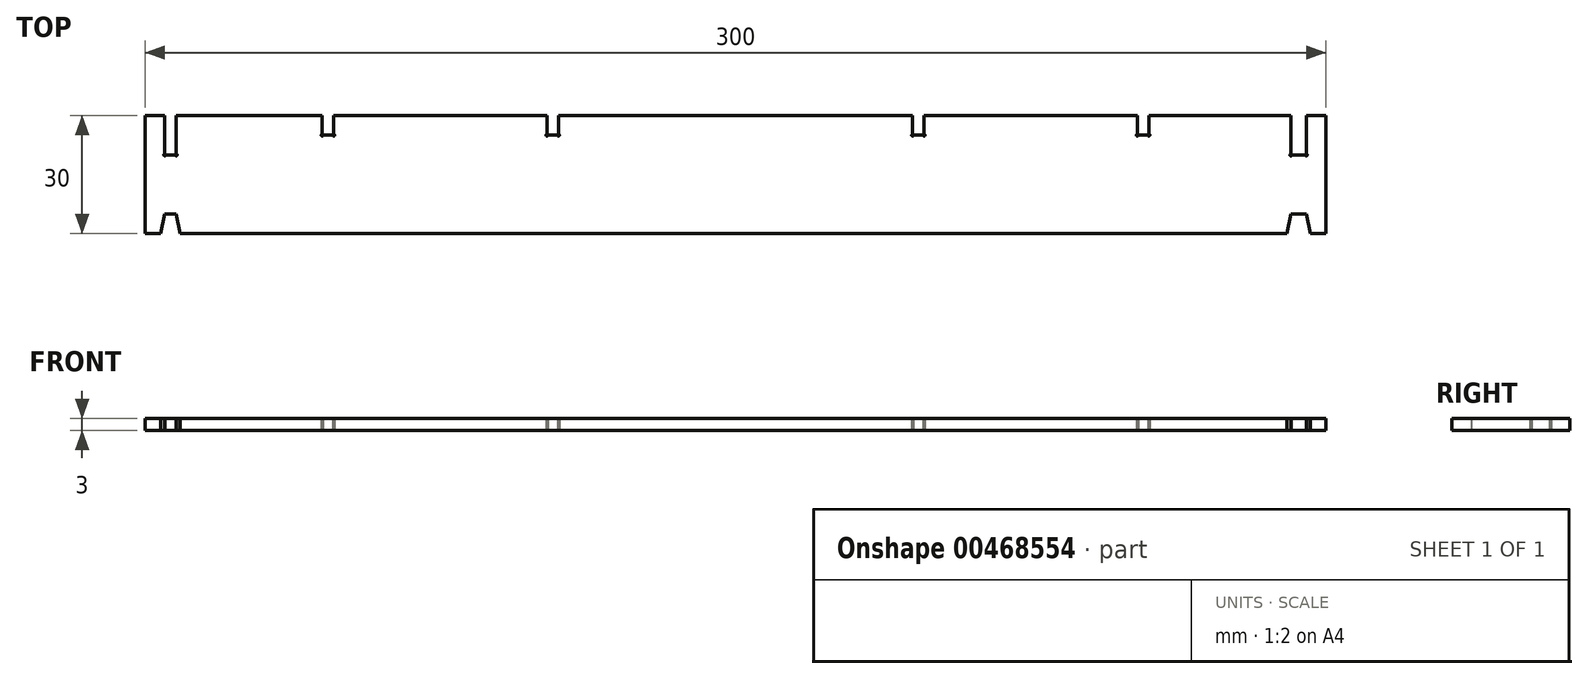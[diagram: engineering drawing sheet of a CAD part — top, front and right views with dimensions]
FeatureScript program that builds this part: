
annotation { "Feature Type Name" : "Feature", "Feature Type Description" : "" }
export const myFeature = defineFeature(function(context is Context, id is Id, definition is map)
    precondition{}
    {
        {
            var Q0;
            Q0=qCreatedBy(makeId("Top.planeOp"),FACE);
            var sketch = newSketch(context, id + "F0", { "sketchPlane" : qUnion([Q0])});
            skLineSegment(sketch, "E0.bottom", {"start": v(-145.05, -9.99) * mm, "end": v(154.95, -9.99) * mm});
            skLineSegment(sketch, "E0.top", {"start": v(-145.05, -39.99) * mm, "end": v(154.95, -39.99) * mm});
            skLineSegment(sketch, "E0.left", {"start": v(-145.05, -9.99) * mm, "end": v(-145.05, -39.99) * mm});
            skLineSegment(sketch, "E0.right", {"start": v(154.95, -9.99) * mm, "end": v(154.95, -39.99) * mm});
            skPoint(sketch, "E1", {"position": v(-100.05, -9.99) * mm});
            skPoint(sketch, "E2", {"position": v(109.95, -9.99) * mm});
            skLineSegment(sketch, "E3", {"start": v(109.95, -9.99) * mm, "end": v(109.95, -14.99) * mm});
            skLineSegment(sketch, "E4", {"start": v(109.95, -14.99) * mm, "end": v(107.05, -14.99) * mm});
            skLineSegment(sketch, "E5", {"start": v(107.05, -14.99) * mm, "end": v(107.05, -9.99) * mm});
            skLineSegment(sketch, "E6", {"start": v(-100.05, -9.99) * mm, "end": v(-100.05, -14.99) * mm});
            skLineSegment(sketch, "E7", {"start": v(-100.05, -14.99) * mm, "end": v(-97.15, -14.99) * mm});
            skLineSegment(sketch, "E8", {"start": v(-97.15, -14.99) * mm, "end": v(-97.15, -9.99) * mm});
            skPoint(sketch, "E9", {"position": v(-40.05, -9.99) * mm});
            skLineSegment(sketch, "E10", {"start": v(-40.05, -9.99) * mm, "end": v(-40.05, -14.99) * mm});
            skLineSegment(sketch, "E11", {"start": v(-40.05, -14.99) * mm, "end": v(-42.95, -14.99) * mm});
            skLineSegment(sketch, "E12", {"start": v(-42.95, -14.99) * mm, "end": v(-42.95, -9.99) * mm});
            skPoint(sketch, "E13", {"position": v(49.95, -9.99) * mm});
            skLineSegment(sketch, "E14", {"start": v(49.95, -9.99) * mm, "end": v(49.95, -14.99) * mm});
            skLineSegment(sketch, "E15", {"start": v(49.95, -14.99) * mm, "end": v(52.85, -14.99) * mm});
            skLineSegment(sketch, "E16", {"start": v(52.85, -14.99) * mm, "end": v(52.85, -9.99) * mm});
            skPoint(sketch, "E17", {"position": v(-140.05, -9.99) * mm});
            skLineSegment(sketch, "E18", {"start": v(-140.05, -9.99) * mm, "end": v(-140.05, -19.99) * mm});
            skLineSegment(sketch, "E19", {"start": v(-140.05, -19.99) * mm, "end": v(-137.15, -19.99) * mm});
            skLineSegment(sketch, "E20", {"start": v(-137.15, -19.99) * mm, "end": v(-137.15, -9.99) * mm});
            skLineSegment(sketch, "E21", {"start": v(149.95, -9.99) * mm, "end": v(149.95, -19.99) * mm});
            skLineSegment(sketch, "E22", {"start": v(149.95, -19.99) * mm, "end": v(146.05, -19.99) * mm});
            skLineSegment(sketch, "E23", {"start": v(146.05, -19.99) * mm, "end": v(146.05, -9.99) * mm});
            skCircle(sketch, "E24", {"center": v(-140.05, -19.99) * mm, "radius": 0.25 * mm});
            skCircle(sketch, "E25", {"center": v(-137.15, -19.99) * mm, "radius": 0.25 * mm});
            skCircle(sketch, "E26", {"center": v(-100.05, -14.99) * mm, "radius": 0.25 * mm});
            skCircle(sketch, "E27", {"center": v(-97.15, -14.99) * mm, "radius": 0.25 * mm});
            skCircle(sketch, "E28", {"center": v(-42.95, -14.99) * mm, "radius": 0.25 * mm});
            skCircle(sketch, "E29", {"center": v(-40.05, -14.99) * mm, "radius": 0.25 * mm});
            skCircle(sketch, "E30", {"center": v(49.95, -14.99) * mm, "radius": 0.25 * mm});
            skCircle(sketch, "E31", {"center": v(52.85, -14.99) * mm, "radius": 0.25 * mm});
            skCircle(sketch, "E32", {"center": v(107.05, -14.99) * mm, "radius": 0.25 * mm});
            skCircle(sketch, "E33", {"center": v(109.95, -14.99) * mm, "radius": 0.25 * mm});
            skCircle(sketch, "E34", {"center": v(146.05, -19.99) * mm, "radius": 0.25 * mm});
            skCircle(sketch, "E35", {"center": v(149.95, -19.99) * mm, "radius": 0.25 * mm});
            skLineSegment(sketch, "E36", {"start": v(-140.05, -9.99) * mm, "end": v(-140.05, -39.99) * mm, "construction": true});
            skLineSegment(sketch, "E37", {"start": v(-137.15, -9.99) * mm, "end": v(-137.15, -39.99) * mm, "construction": true});
            skLineSegment(sketch, "E38", {"start": v(149.95, -9.99) * mm, "end": v(149.95, -39.99) * mm, "construction": true});
            skLineSegment(sketch, "E39", {"start": v(146.05, -9.99) * mm, "end": v(146.05, -39.99) * mm, "construction": true});
            skLineSegment(sketch, "E40", {"start": v(150.95, -39.99) * mm, "end": v(149.95, -34.99) * mm});
            skLineSegment(sketch, "E41", {"start": v(149.95, -34.99) * mm, "end": v(146.05, -34.99) * mm});
            skLineSegment(sketch, "E42", {"start": v(146.05, -34.99) * mm, "end": v(145.05, -39.99) * mm});
            skLineSegment(sketch, "E43", {"start": v(-141.05, -39.99) * mm, "end": v(-140.05, -34.99) * mm});
            skLineSegment(sketch, "E44", {"start": v(-140.05, -34.99) * mm, "end": v(-137.15, -34.99) * mm});
            skLineSegment(sketch, "E45", {"start": v(-137.15, -34.99) * mm, "end": v(-136.15, -39.99) * mm});
            skSolve(sketch);
        }
        {
            var Q0;
            Q0=makeQuery(id+"F0.imprint","IMPRINT",FACE,{"disambiguationData":[TD([[makeQuery(id+"F0.imprint","IMPRINT",EDGE,{"derivedFrom":sQuery(id+"F0.wireOp",EDGE,"E0.top")}),1.0]])]});
            extrude(context, id + "F1", {"entities" : qUnion([Q0]), "depth" : 3 * mm, "offsetDistance" : 25 * mm});
        }
    });
